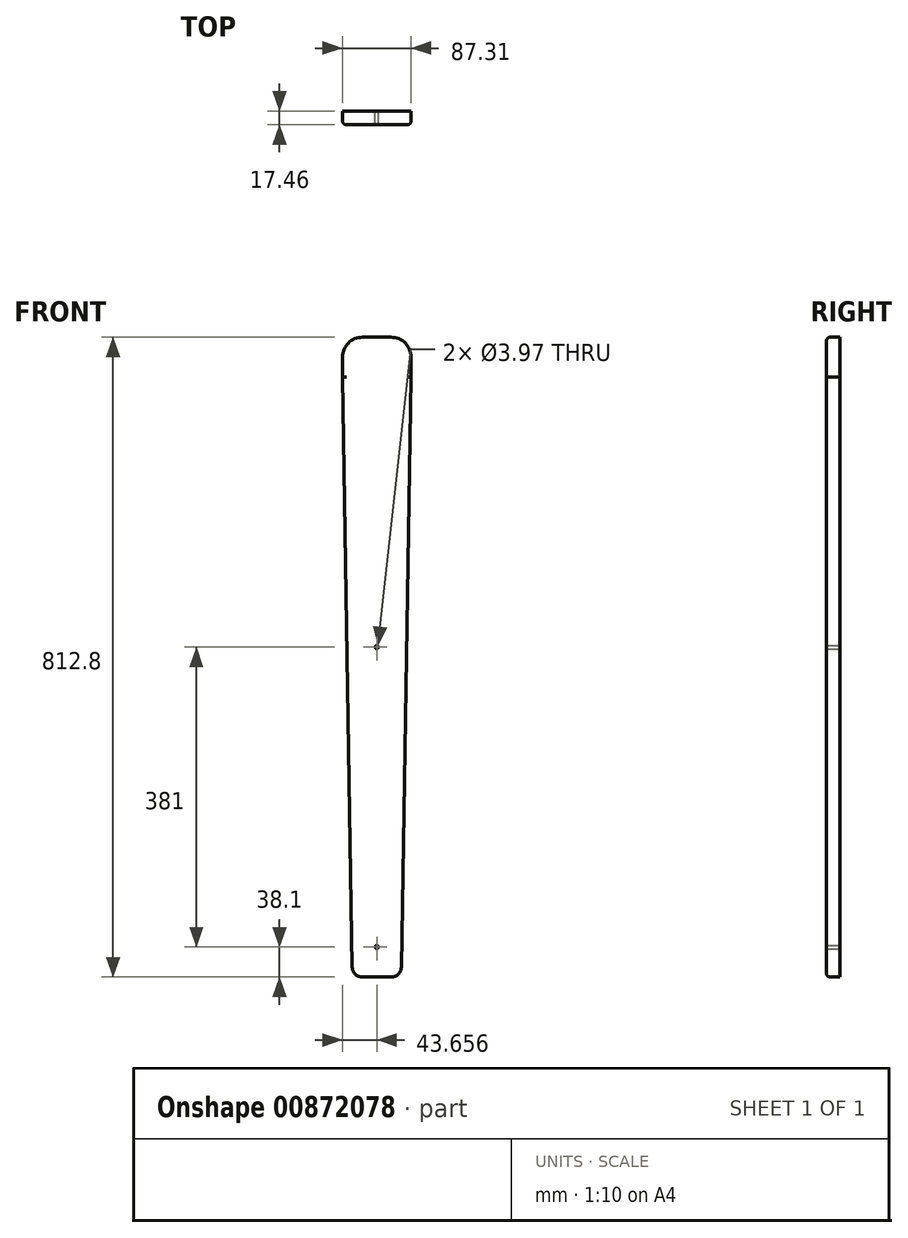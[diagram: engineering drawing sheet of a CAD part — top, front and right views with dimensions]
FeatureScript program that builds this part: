
annotation { "Feature Type Name" : "Feature", "Feature Type Description" : "" }
export const myFeature = defineFeature(function(context is Context, id is Id, definition is map)
    precondition{}
    {
        {
            var Q0;
            Q0=qCreatedBy(makeId("Front.planeOp"),FACE);
            var sketch = newSketch(context, id + "F0", { "sketchPlane" : qUnion([Q0])});
            skLineSegment(sketch, "E0.top", {"start": v(25.4, 812.8) * mm, "end": v(61.91, 812.8) * mm});
            skPoint(sketch, "E1.visualSharp", {"position": v(0, 812.8) * mm});
            skArc(sketch, "E1.filletArc", {"start": v(25.4, 812.8) * mm, "mid": v(7.44, 805.36) * mm, "end": v(0, 787.4) * mm});
            skPoint(sketch, "E2.visualSharp", {"position": v(87.31, 812.8) * mm});
            skArc(sketch, "E2.filletArc", {"start": v(87.31, 787.4) * mm, "mid": v(79.87, 805.36) * mm, "end": v(61.91, 812.8) * mm});
            skLineSegment(sketch, "E3", {"start": v(0, 787.4) * mm, "end": v(0, 762) * mm});
            skLineSegment(sketch, "E4", {"start": v(87.31, 787.4) * mm, "end": v(87.31, 762) * mm});
            skLineSegment(sketch, "E5", {"start": v(0, 762) * mm, "end": v(12.5, 12.49) * mm});
            skLineSegment(sketch, "E6", {"start": v(25.2, 0) * mm, "end": v(62.12, 0) * mm});
            skLineSegment(sketch, "E7", {"start": v(74.82, 12.49) * mm, "end": v(87.31, 762) * mm});
            skLineSegment(sketch, "E8", {"start": v(87.31, 812.8) * mm, "end": v(61.91, 812.8) * mm, "construction": true});
            skLineSegment(sketch, "E9", {"start": v(25.4, 812.8) * mm, "end": v(0, 812.8) * mm, "construction": true});
            skLineSegment(sketch, "E10", {"start": v(0, 812.8) * mm, "end": v(0, 787.4) * mm, "construction": true});
            skLineSegment(sketch, "E11", {"start": v(87.31, 812.8) * mm, "end": v(87.31, 787.4) * mm, "construction": true});
            skLineSegment(sketch, "E12", {"start": v(0, 762) * mm, "end": v(0, 0) * mm, "construction": true});
            skLineSegment(sketch, "E13", {"start": v(87.31, 762) * mm, "end": v(87.31, 0) * mm, "construction": true});
            skPoint(sketch, "E14.visualSharp", {"position": v(12.7, 0) * mm});
            skArc(sketch, "E14.filletArc", {"start": v(12.5, 12.49) * mm, "mid": v(16.28, 3.65) * mm, "end": v(25.2, 0) * mm});
            skPoint(sketch, "E15.visualSharp", {"position": v(74.61, 0) * mm});
            skArc(sketch, "E15.filletArc", {"start": v(62.12, 0) * mm, "mid": v(71.03, 3.65) * mm, "end": v(74.82, 12.49) * mm});
            skLineSegment(sketch, "E16", {"start": v(0, 0) * mm, "end": v(25.2, 0) * mm, "construction": true});
            skLineSegment(sketch, "E17", {"start": v(62.12, 0) * mm, "end": v(87.31, 0) * mm, "construction": true});
            skCircle(sketch, "E18", {"center": v(43.66, 38.1) * mm, "radius": 1.98 * mm});
            skPoint(sketch, "E18.centerSnap0", {"position": v(43.66, 0) * mm});
            skCircle(sketch, "E19", {"center": v(43.66, 419.1) * mm, "radius": 1.98 * mm});
            skSolve(sketch);
        }
        {
            var Q0;
            Q0=qSketchRegion(id+"F0",true);
            extrude(context, id + "F1", {"entities" : qUnion([Q0]), "depth" : 17.46 * mm});
        }
        {
            var Q0;
            Q0=makeQuery(id+"F1.opExtrude","CAP_EDGE",EDGE,{"disambiguationData":[OSD([sQuery(id+"F0.wireOp",EDGE,"E5")])],"isStart":false});
            var Q1;
            Q1=makeQuery(id+"F1.opExtrude","CAP_EDGE",EDGE,{"disambiguationData":[OSD([sQuery(id+"F0.wireOp",EDGE,"E1.filletArc")])],"isStart":false});
            fillet(context, id + "F2", {"entities" : qUnion([Q0, Q1]), "radius" : 5.08 * mm, "tangentPropagation" : true, "allowEdgeOverflow" : false});
        }
    });
